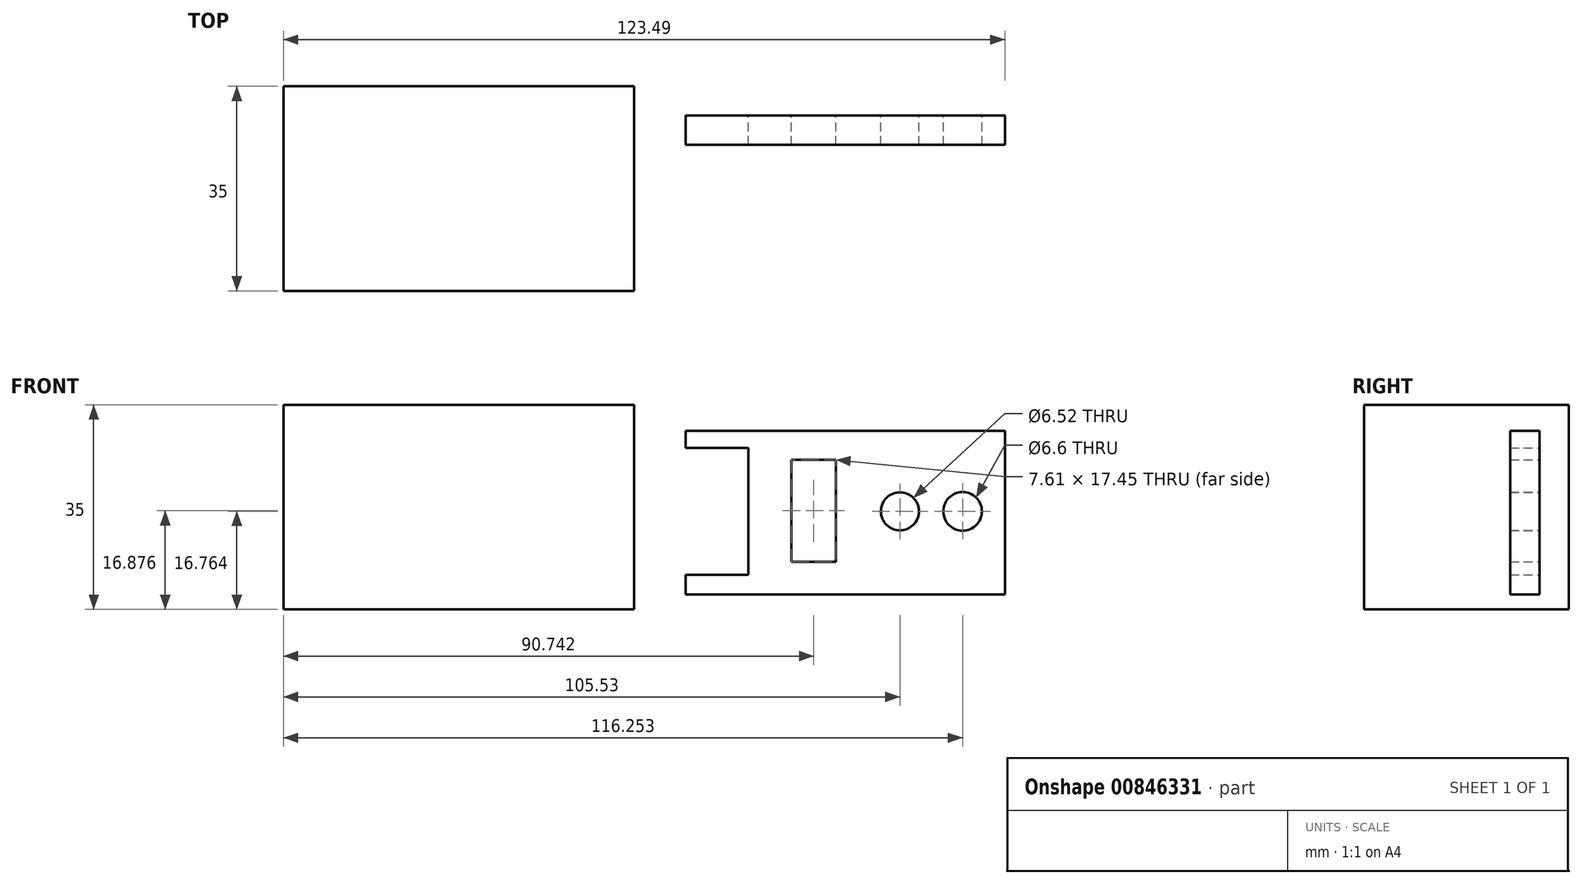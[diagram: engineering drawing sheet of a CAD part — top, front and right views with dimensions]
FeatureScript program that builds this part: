
annotation { "Feature Type Name" : "Feature", "Feature Type Description" : "" }
export const myFeature = defineFeature(function(context is Context, id is Id, definition is map)
    precondition{}
    {
        {
            var Q0;
            Q0=qCreatedBy(makeId("Front.planeOp"),FACE);
            var sketch = newSketch(context, id + "F0", { "sketchPlane" : qUnion([Q0])});
            skLineSegment(sketch, "E0.bottom", {"start": v(-50.36, 22.71) * mm, "end": v(9.64, 22.71) * mm});
            skLineSegment(sketch, "E0.top", {"start": v(-50.36, -12.29) * mm, "end": v(9.64, -12.29) * mm});
            skLineSegment(sketch, "E0.left", {"start": v(-50.36, 22.71) * mm, "end": v(-50.36, -12.29) * mm});
            skLineSegment(sketch, "E0.right", {"start": v(9.64, 22.71) * mm, "end": v(9.64, -12.29) * mm});
            skSolve(sketch);
        }
        {
            var Q0;
            Q0=makeQuery(id+"F0.imprint","IMPRINT",FACE,{"disambiguationData":[TD([[makeQuery(id+"F0.imprint","IMPRINT",EDGE,{"derivedFrom":sQuery(id+"F0.wireOp",EDGE,"E0.bottom")}),-1.0]])]});
            extrude(context, id + "F1", {"entities" : qUnion([Q0]), "depth" : 35 * mm, "offsetDistance" : 25 * mm});
        }
        {
            var Q0;
            Q0=qCreatedBy(makeId("Front.planeOp"),FACE);
            cPlane(context, id + "F2", {"entities" : qUnion([Q0]), "cplaneType" : CPlaneType.OFFSET, "offset" : 5 * mm, "width" : 150 * mm, "height" : 150 * mm});
        }
        {
            var Q0;
            Q0=qCreatedBy(id+"F2.planeOp",FACE);
            var sketch = newSketch(context, id + "F3", { "sketchPlane" : qUnion([Q0])});
            skLineSegment(sketch, "E1", {"start": v(18.46, 18.23) * mm, "end": v(18.46, 15.32) * mm});
            skLineSegment(sketch, "E2", {"start": v(18.46, 15.32) * mm, "end": v(29.2, 15.32) * mm});
            skLineSegment(sketch, "E3", {"start": v(29.2, 15.32) * mm, "end": v(29.2, -6.38) * mm});
            skLineSegment(sketch, "E4", {"start": v(29.2, -6.38) * mm, "end": v(18.46, -6.38) * mm});
            skLineSegment(sketch, "E5", {"start": v(18.46, -6.38) * mm, "end": v(18.46, -9.73) * mm});
            skLineSegment(sketch, "E6", {"start": v(18.46, -9.73) * mm, "end": v(73.13, -9.73) * mm});
            skLineSegment(sketch, "E7", {"start": v(73.13, -9.73) * mm, "end": v(73.13, 18.23) * mm});
            skLineSegment(sketch, "E8", {"start": v(73.13, 18.23) * mm, "end": v(18.46, 18.23) * mm});
            skLineSegment(sketch, "E9.bottom", {"start": v(36.58, 13.31) * mm, "end": v(44.19, 13.31) * mm});
            skLineSegment(sketch, "E9.top", {"start": v(36.58, -4.14) * mm, "end": v(44.19, -4.14) * mm});
            skLineSegment(sketch, "E9.left", {"start": v(36.58, 13.31) * mm, "end": v(36.58, -4.14) * mm});
            skLineSegment(sketch, "E9.right", {"start": v(44.19, 13.31) * mm, "end": v(44.19, -4.14) * mm});
            skCircle(sketch, "E10", {"center": v(55.17, 4.47) * mm, "radius": 3.26 * mm});
            skPoint(sketch, "E11", {"position": v(29.2, 4.47) * mm});
            skCircle(sketch, "E12", {"center": v(65.9, 4.47) * mm, "radius": 3.3 * mm});
            skSolve(sketch);
        }
        {
            var Q0;
            Q0=makeQuery(id+"F3.imprint","IMPRINT",FACE,{"disambiguationData":[TD([[makeQuery(id+"F3.imprint","IMPRINT",EDGE,{"derivedFrom":sQuery(id+"F3.wireOp",EDGE,"E1")}),1.0]])]});
            extrude(context, id + "F4", {"entities" : qUnion([Q0]), "depth" : 5 * mm, "offsetDistance" : 25 * mm});
        }
    });
